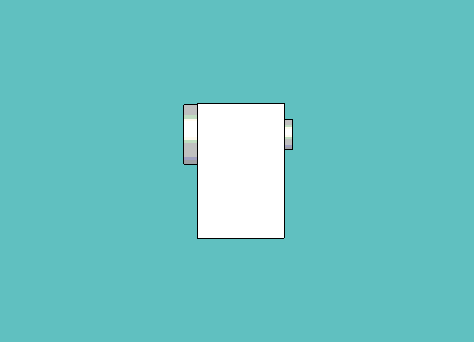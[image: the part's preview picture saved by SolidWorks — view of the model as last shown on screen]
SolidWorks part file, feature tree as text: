
SOLIDWORKS PART (.sldprt)
format: sldprt  version: not decoded by parser v0  size: 240,128 bytes
history: native  units: mm
features: sketch x6, extrude x3, cut_extrude x2, material x1, plane x1 (+11 scaffold rows collapsed)
feature tree (24):
  scaffold x11  (default folders/planes/origin — collapsed)
  material  "Material <not specified>"
  sketch  "Sketch1"  dims[D1=11.5062mm D2=49.9364mm D3=32.004mm]
  extrude  "Extrude1"  Depth=32.004mm
  sketch  "Sketch2"  dims[D1=10.7696mm]
  extrude  "Extrude2"  Depth=2.99085mm
  sketch  "Sketch3"  dims[D1=3.5052mm]
  cut_extrude  "Cut-Extrude1"  Depth=11.9888mm
  sketch  "Sketch6"  dims[D1=21.8948mm]
  extrude  "Extrude3"  Depth=5.0038mm
  sketch  "Sketch5"  dims[D1=5.9944mm]
  cut_extrude  "Cut-Extrude2"  Depth=8.9916mm
  sketch  "Sketch7"
  plane  "Plane1"
decode coverage: 10 of 11 modeling features carry decoded parameters
note: suppression state not decoded; provenance and decode notes live in map.json
